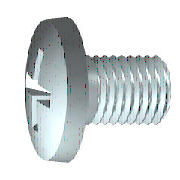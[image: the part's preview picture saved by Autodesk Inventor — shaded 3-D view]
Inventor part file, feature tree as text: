
AUTODESK INVENTOR PART (.ipt)
format: ipt  version: 2015 (Build 190159000, 159)  size: 239,104 bytes
history: native  units: mm (DEFAULTED — no unit token found)
features: chamfer x4, other x3, sketch x2, revolve x1, fillet x1, extrude x1, pattern_circular x1
ambient origin geometry x8: Origin, YZ Plane, XZ Plane, XY Plane, X Axis, Y Axis, Z Axis, Center Point
bodies: Solid1 (feature_tree)
feature tree (13):
  revolve  "Revolution1"  [1 undecoded]
  chamfer  "Chamfer1"  Distance=0.125mm
  chamfer  "Chamfer2"  Distance=0.125mm
  fillet  "Fillet1"  Radius=0.25mm
  extrude  "Extrusion1"  Depth=10.0mm
  pattern_circular  "PolarArray1"  [2 undecoded]
  chamfer  "Chamfer3"  Distance=1.612mm
  chamfer  "Chamfer4"  Distance=0.62mm
  other  "MSC_A1"
  other  "MSC_PF1"
  other  "MSC_PT1"
  sketch  "Sketch2"  dims[d6=2.75mm d9=0.872665mm]
  sketch  "Sketch3"  dims[d10=90.0deg d11=0.125mm d12=0.125mm d13=0.25mm d14=0.25mm d16=10.0mm d17=0.0mm d19=1.612mm d20=0.62mm d21=2.52mm d22=0.516667mm d23=0.0mm d24=40.0mm d26=360.0deg d28=0.0mm d29=0.0mm d30=0.442857mm d31=0.442857mm d32=0.206667mm d33=0.206667mm d34=45.0deg d35=45.0deg d36=45.0deg d37=45.0deg d38=0.0mm d39=0.0mm d40=0.0mm]
note: 3 required parameter values undecoded (feature->parameter linkage not recoverable at this tier; creation-order binding heuristic only, values carry confidence <= 0.55)